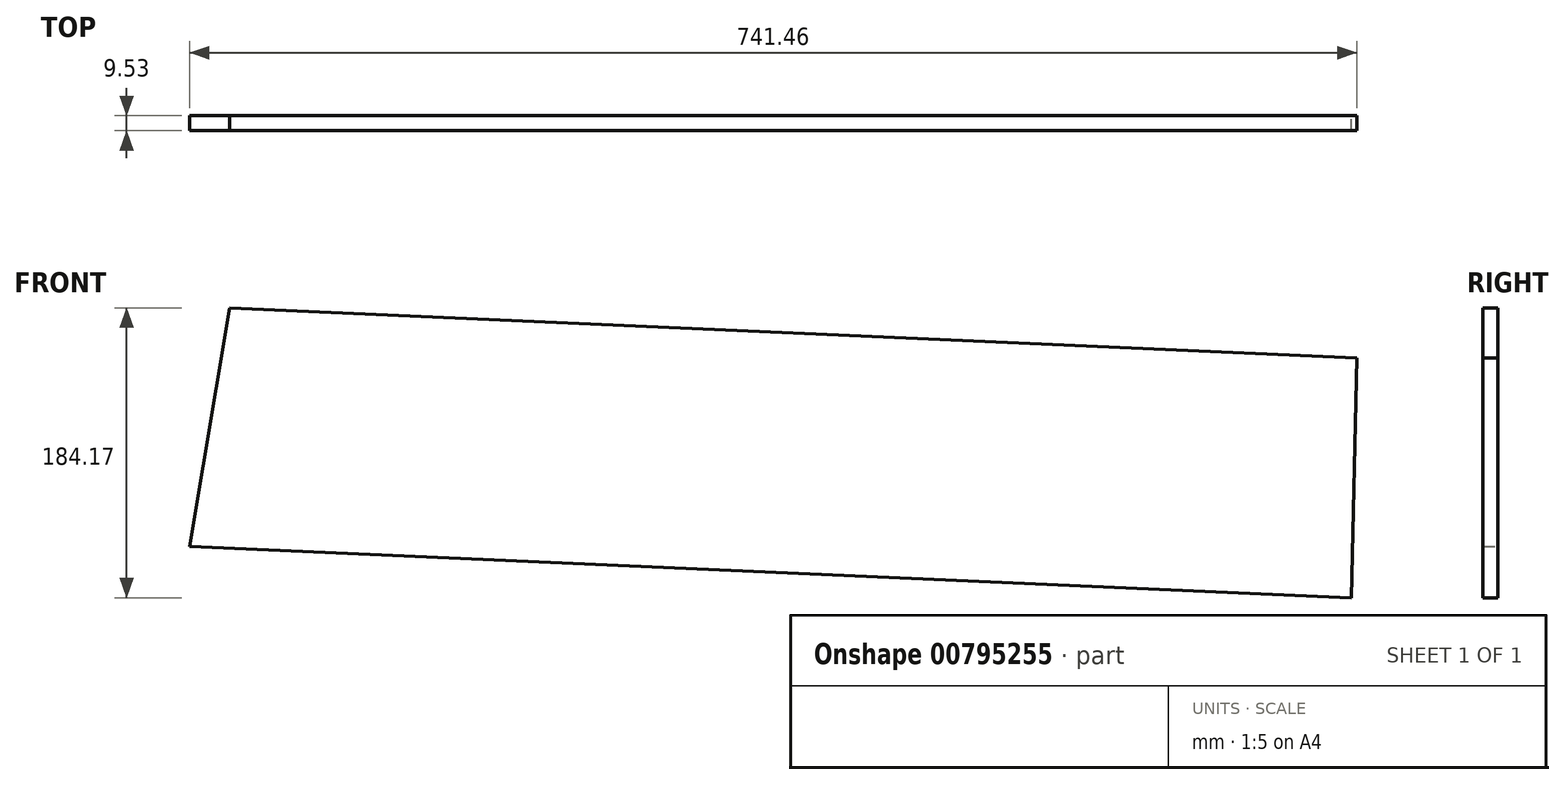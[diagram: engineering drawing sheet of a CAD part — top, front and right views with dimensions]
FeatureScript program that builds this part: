
annotation { "Feature Type Name" : "Feature", "Feature Type Description" : "" }
export const myFeature = defineFeature(function(context is Context, id is Id, definition is map)
    precondition{}
    {
        {
            var Q0;
            Q0=qCreatedBy(makeId("Front.planeOp"),FACE);
            var sketch = newSketch(context, id + "F0", { "sketchPlane" : qUnion([Q0])});
            skLineSegment(sketch, "E0", {"start": v(329.09, -76.96) * mm, "end": v(332.47, 75.44) * mm});
            skLineSegment(sketch, "E1", {"start": v(332.47, 75.44) * mm, "end": v(-383.56, 107.21) * mm});
            skLineSegment(sketch, "E2", {"start": v(-383.56, 107.21) * mm, "end": v(-409, -44.21) * mm});
            skLineSegment(sketch, "E3", {"start": v(-409, -44.21) * mm, "end": v(329.09, -76.96) * mm});
            skSolve(sketch);
        }
        {
            var Q0;
            Q0 = qSketchRegion(id + "F0", true);
            extrude(context, id + "F1", {"entities" : qUnion([Q0]), "depth" : 9.52 * mm, "offsetDistance" : 25.4 * mm});
        }
    });
